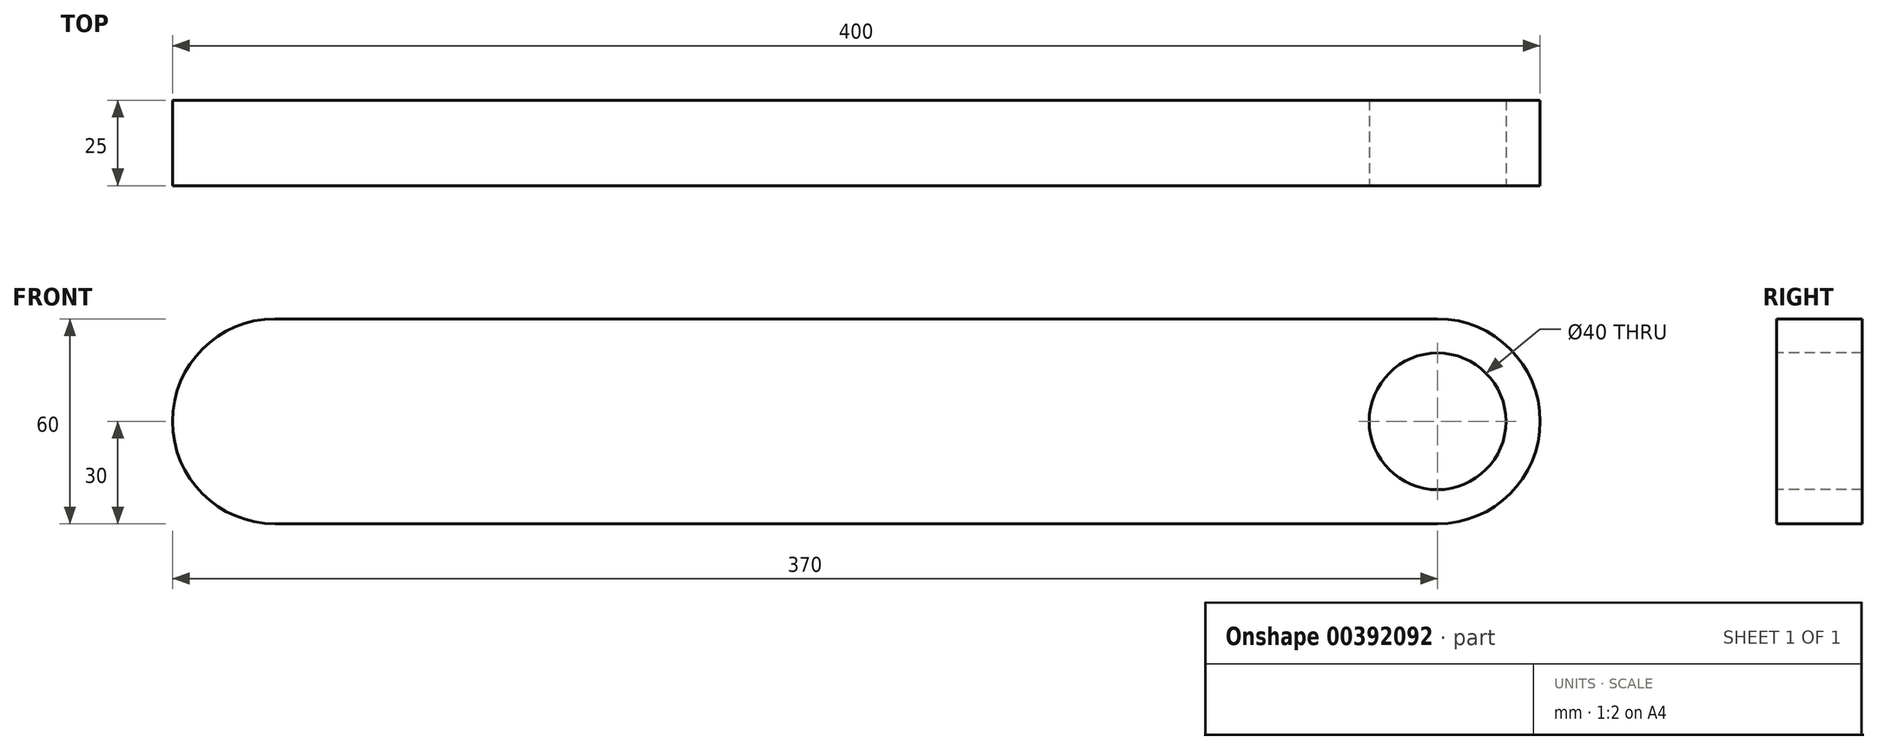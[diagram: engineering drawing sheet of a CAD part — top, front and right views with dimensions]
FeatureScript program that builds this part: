
annotation { "Feature Type Name" : "Feature", "Feature Type Description" : "" }
export const myFeature = defineFeature(function(context is Context, id is Id, definition is map)
    precondition{}
    {
        {
            var Q0;
            Q0=qCreatedBy(makeId("Front.planeOp"),FACE);
            var sketch = newSketch(context, id + "F0", { "sketchPlane" : qUnion([Q0])});
            skLineSegment(sketch, "E0.bottom", {"start": v(200, -30) * mm, "end": v(-200, -30) * mm});
            skLineSegment(sketch, "E0.top", {"start": v(200, 30) * mm, "end": v(-200, 30) * mm});
            skLineSegment(sketch, "E0.left", {"start": v(200, -30) * mm, "end": v(200, 30) * mm});
            skLineSegment(sketch, "E0.right", {"start": v(-200, -30) * mm, "end": v(-200, 30) * mm});
            skPoint(sketch, "E0.middle", {"position": v(0, 0) * mm});
            skSolve(sketch);
        }
        {
            var Q0;
            Q0 = qSketchRegion(id + "F0", true);
            extrude(context, id + "F1", {"entities" : qUnion([Q0]), "depth" : 25 * mm});
        }
        {
            var Q0;
            Q0=makeQuery(id+"F1.opExtrude","SWEPT_EDGE",EDGE,{"disambiguationData":[OSD([sQuery(id+"F0.wireOp",EDGE,"E0.top"),sQuery(id+"F0.wireOp",EDGE,"E0.right")])]});
            var Q1;
            Q1=makeQuery(id+"F1.opExtrude","SWEPT_EDGE",EDGE,{"disambiguationData":[OSD([sQuery(id+"F0.wireOp",EDGE,"E0.bottom"),sQuery(id+"F0.wireOp",EDGE,"E0.right")])]});
            var Q2;
            Q2=makeQuery(id+"F1.opExtrude","SWEPT_EDGE",EDGE,{"disambiguationData":[OSD([sQuery(id+"F0.wireOp",EDGE,"E0.top"),sQuery(id+"F0.wireOp",EDGE,"E0.left")])]});
            var Q3;
            Q3=makeQuery(id+"F1.opExtrude","SWEPT_EDGE",EDGE,{"disambiguationData":[OSD([sQuery(id+"F0.wireOp",EDGE,"E0.bottom"),sQuery(id+"F0.wireOp",EDGE,"E0.left")])]});
            fillet(context, id + "F2", {"entities" : qUnion([Q0, Q1, Q2, Q3]), "radius" : 30 * mm, "tangentPropagation" : true, "allowEdgeOverflow" : false});
        }
        {
            var Q0;
            Q0=makeQuery(id+"F1.opExtrude","CAP_FACE",FACE,{"disambiguationData":[OSD([sQuery(id+"F0.wireOp",EDGE,"E0.bottom"),sQuery(id+"F0.wireOp",EDGE,"E0.top"),sQuery(id+"F0.wireOp",EDGE,"E0.left"),sQuery(id+"F0.wireOp",EDGE,"E0.right")])],"isStart":false});
            var sketch = newSketch(context, id + "F3", { "sketchPlane" : qUnion([Q0])});
            skLineSegment(sketch, "E1", {"start": v(0, 0) * mm, "end": v(170, 0) * mm});
            skCircle(sketch, "E2", {"center": v(170, 0) * mm, "radius": 20 * mm});
            skPoint(sketch, "E3.center.orphan", {"position": v(190, 0) * mm});
            skSolve(sketch);
        }
        {
            var Q0;
            Q0=makeQuery(id+"F3.imprint","IMPRINT",FACE,{"disambiguationData":[TD([[makeQuery(id+"F3.imprint","IMPRINT",EDGE,{"derivedFrom":sQuery(id+"F3.wireOp",EDGE,"E2")}),1.0]])]});
            extrude(context, id + "F4", {"entities" : qUnion([Q0]), "operationType" : NewBodyOperationType.REMOVE, "oppositeDirection" : true, "depth" : 25 * mm});
        }
    });
